# Revit family: FP_Revit_18_RS2484VL2K1_Wine_Column_90001065A
name_source: partatom
category: Specialty Equipment
revit_build: Autodesk Revit 2018 (Build: 20170223_1515(x64)
units: mm (PartAtom-declared; Revit-internal decimal feet)

## family parameters
Always vertical = Yes
Cut with Voids When Loaded = Yes
OmniClass Number = 23.40.40.11.11
OmniClass Title = Refrigerators and Freezers
Part Type = Normal
Room Calculation Point = No
Round Connector Dimension = Use Diameter
Shared = No
Work Plane-Based = No

## types (1)
- FP_Revit_18_RS2484VL2K1_Wine_Column_90001065A
    Cavity - Depth = 635 mm
    Cavity - Height = 2134 mm  [stored 7.00131 ft]
    Cavity - Width = 610 mm  [stored 2.00131 ft]
    Connector Description - Electrical = 120 V, 10 amp fused electrical supply
    Description = 24" Integrated Column Wine Cabinet
    Handle Style - Contemporary Round (AHS-RD84) = No
    Handle Style - Contemporary Square (AHD3-RD84) = No
    Handle Style - Professional Round (AHC-RD84) = No
    Handle Style - Professional Square (AHV2-RD84) = No
    Manufacturer = Fisher & Paykel Appliances
    Material - Body = Fisher & Paykel - Grey
    Material - Door Front = Fisher & Paykel - Stainless Steel
    Material - Door Structure = Fisher & Paykel - White
    Material - Handle = Fisher & Paykel - Aluminium
    Model = RS2484VL2K1
    Product - Depth (exl front panel) = 610 mm  [stored 2.00131 ft]
    Product - Height = 2134 mm  [stored 7.00131 ft]
    Product - Width = 603 mm  [stored 1.97835 ft]
    Stainless Steel Door Panels (RD2484VL4D) = No
    URL = www.fisherpaykel.com
    Visibility - Clearance Required = Yes
    Visibility - Visibility Control Note = Yes
    Visibility - Water Connection = Yes

note: [stored X ft] marks values corroborated as IEEE doubles in the binary element streams (Revit-internal decimal feet)

## geometry (parser evidence)
native form markers: Sweep x12
no freeform markers — native parametric forms only
